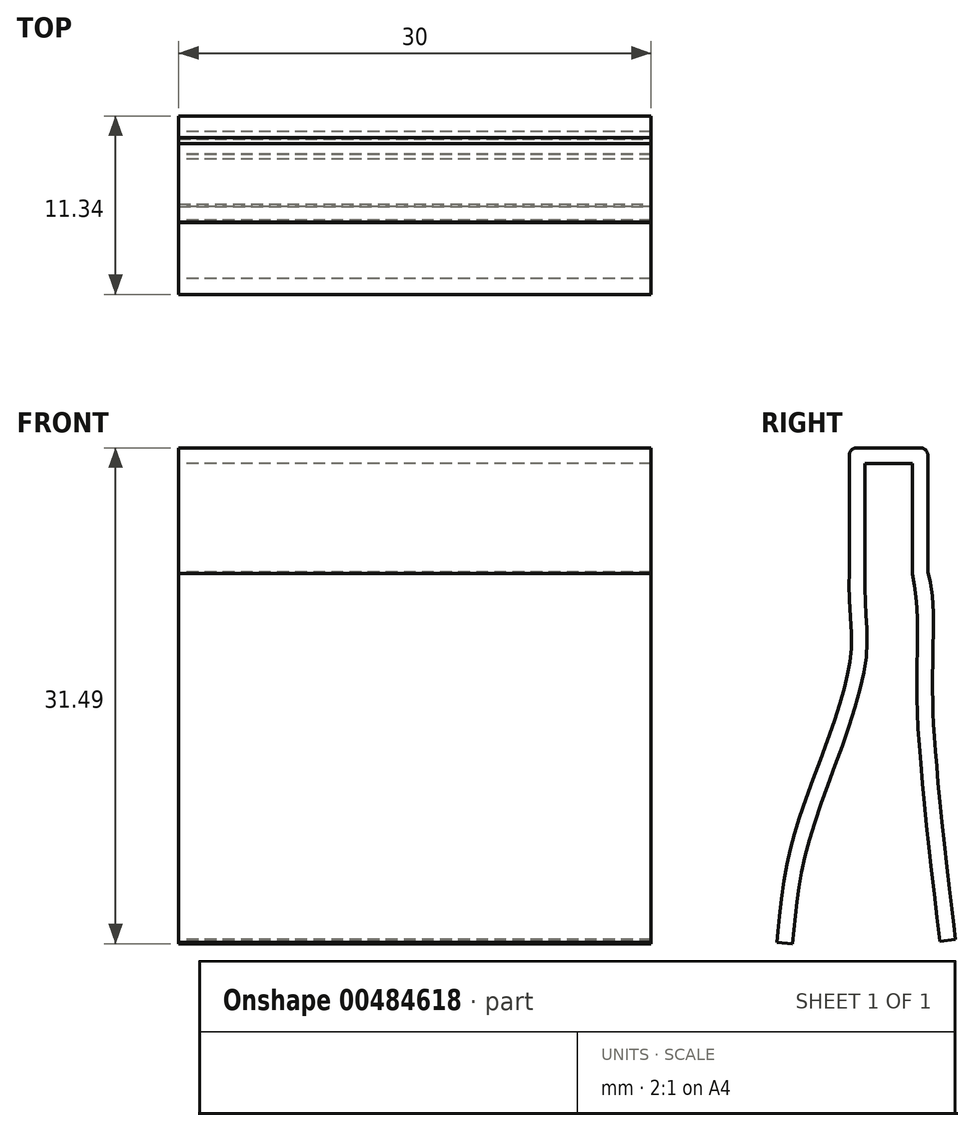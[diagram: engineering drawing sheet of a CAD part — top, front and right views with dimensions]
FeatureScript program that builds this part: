
annotation { "Feature Type Name" : "Feature", "Feature Type Description" : "" }
export const myFeature = defineFeature(function(context is Context, id is Id, definition is map)
    precondition{}
    {
        {
            var Q0;
            Q0=qCreatedBy(makeId("Right.planeOp"),FACE);
            var sketch = newSketch(context, id + "F0", { "sketchPlane" : qUnion([Q0])});
            skLineSegment(sketch, "E0", {"start": v(1.6, 38.03) * mm, "end": v(4.6, 38.03) * mm});
            skLineSegment(sketch, "E1", {"start": v(1.6, 38.03) * mm, "end": v(1.6, 31.03) * mm});
            skLineSegment(sketch, "E2", {"start": v(4.6, 38.03) * mm, "end": v(4.6, 31.03) * mm});
            skFitSpline(sketch, "E3", {"points": [v(1.6, 31.03) * mm, v(1.6, 25.14) * mm, v(-1.88, 14.28) * mm, v(-2.99, 7.54) * mm], "startDerivative": vector(-1.2, -21.66) * mm, "endDerivative": vector(-1.97, -20.56) * mm});
            skFitSpline(sketch, "E4", {"points": [v(4.6, 31.03) * mm, v(4.94, 26.8) * mm, v(4.94, 22.13) * mm, v(6.37, 7.7) * mm], "startDerivative": vector(3.84, -16.77) * mm, "endDerivative": vector(4.27, -34.77) * mm});
            skFitSpline(sketch, "E5.0", {"points": [v(5.58, 31.26) * mm, v(5.76, 30.5) * mm, v(5.94, 28.98) * mm, v(5.95, 26.85) * mm, v(5.9, 25.28) * mm, v(5.9, 23.9) * mm, v(5.9, 22.93) * mm, v(5.94, 22.06) * mm, v(6, 21.12) * mm, v(6.08, 19.82) * mm, v(6.22, 18.08) * mm, v(6.46, 15.57) * mm, v(6.84, 12.16) * mm, v(7.18, 9.27) * mm, v(7.36, 7.82) * mm]});
            skFitSpline(sketch, "E5.1", {"points": [v(0.61, 31.09) * mm, v(0.58, 30.6) * mm, v(0.59, 29.68) * mm, v(0.68, 28.44) * mm, v(0.75, 27.27) * mm, v(0.74, 26.29) * mm, v(0.65, 25.45) * mm, v(0.54, 24.77) * mm, v(0.37, 24.03) * mm, v(0.09, 23) * mm, v(-0.36, 21.6) * mm, v(-1, 19.84) * mm, v(-1.65, 18.05) * mm, v(-2.3, 16.29) * mm, v(-2.75, 14.88) * mm, v(-3.05, 13.8) * mm, v(-3.3, 12.78) * mm, v(-3.54, 11.57) * mm, v(-3.73, 10.2) * mm, v(-3.87, 8.9) * mm, v(-3.94, 8.06) * mm, v(-3.98, 7.63) * mm]});
            skLineSegment(sketch, "E5.2", {"start": v(0.6, 38.53) * mm, "end": v(0.6, 31.06) * mm});
            skLineSegment(sketch, "E5.3", {"start": v(1.1, 39.03) * mm, "end": v(5.1, 39.03) * mm});
            skLineSegment(sketch, "E5.4", {"start": v(5.6, 38.53) * mm, "end": v(5.6, 31.14) * mm});
            skPoint(sketch, "E6.visualSharp", {"position": v(0.6, 39.03) * mm});
            skArc(sketch, "E6.filletArc", {"start": v(1.1, 39.03) * mm, "mid": v(0.76, 38.89) * mm, "end": v(0.6, 38.53) * mm});
            skPoint(sketch, "E7.visualSharp", {"position": v(5.6, 39.03) * mm});
            skArc(sketch, "E7.filletArc", {"start": v(5.6, 38.53) * mm, "mid": v(5.46, 38.89) * mm, "end": v(5.1, 39.03) * mm});
            skLineSegment(sketch, "E8", {"start": v(-3.98, 7.63) * mm, "end": v(-2.99, 7.54) * mm});
            skLineSegment(sketch, "E9", {"start": v(6.37, 7.7) * mm, "end": v(7.36, 7.82) * mm});
            skSolve(sketch);
        }
        {
            var Q0;
            Q0 = qSketchRegion(id + "F0", true);
            extrude(context, id + "F1", {"entities" : qUnion([Q0]), "depth" : 30 * mm, "offsetDistance" : 25 * mm});
        }
    });
